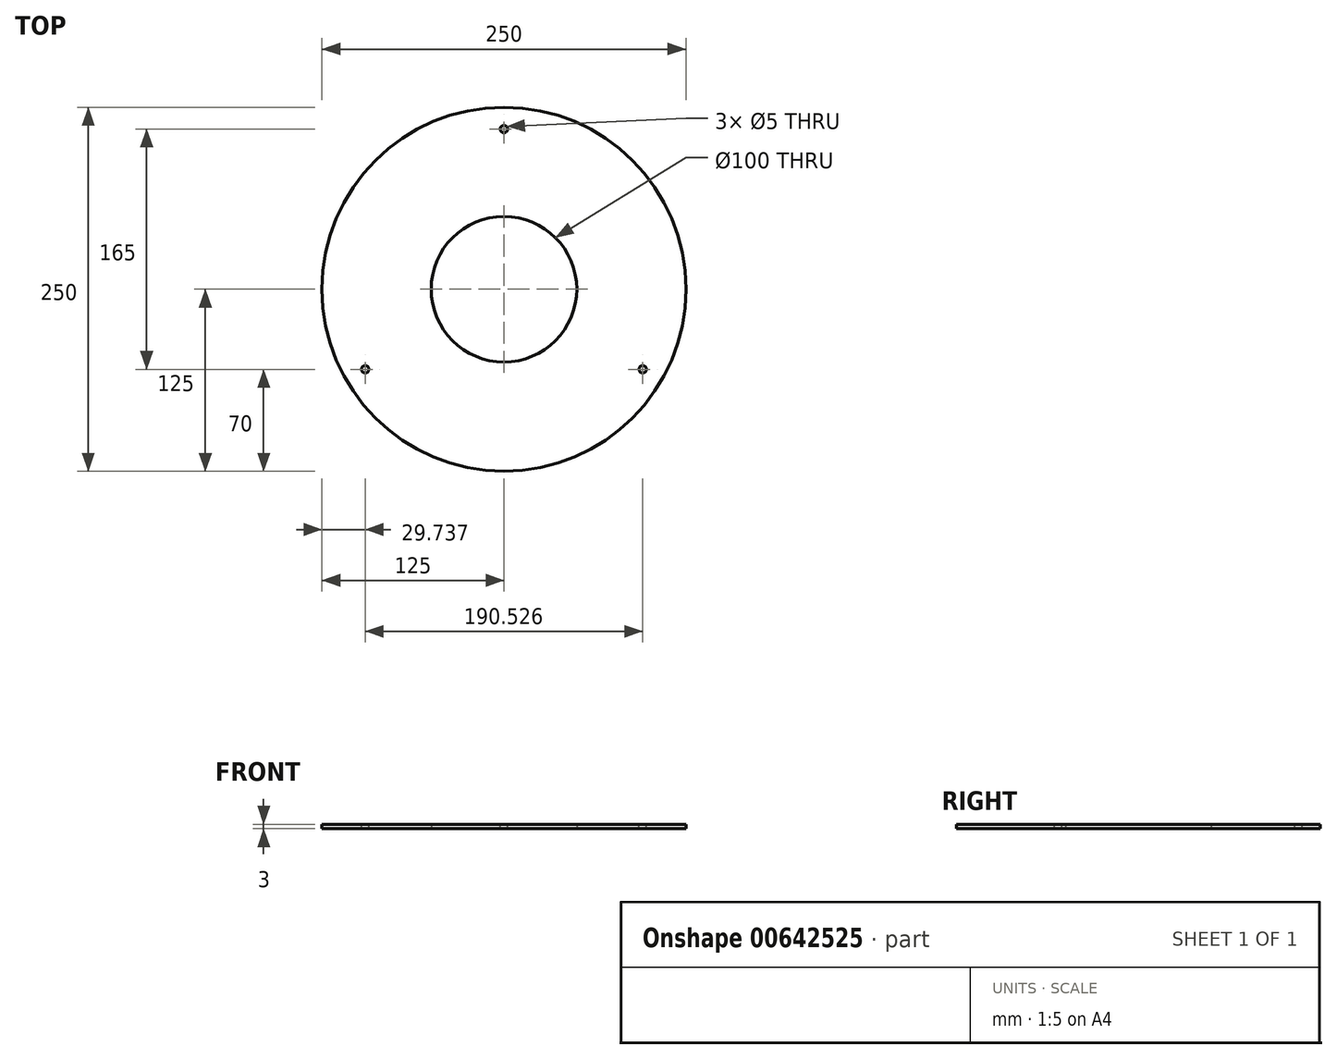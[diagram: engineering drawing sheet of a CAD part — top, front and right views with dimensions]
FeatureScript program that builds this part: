
annotation { "Feature Type Name" : "Feature", "Feature Type Description" : "" }
export const myFeature = defineFeature(function(context is Context, id is Id, definition is map)
    precondition{}
    {
        {
            var Q0;
            Q0=qCreatedBy(makeId("Top.planeOp"),FACE);
            var sketch = newSketch(context, id + "F0", { "sketchPlane" : qUnion([Q0])});
            skCircle(sketch, "E0", {"center": v(0, 0) * mm, "radius": 125 * mm});
            skCircle(sketch, "E1", {"center": v(0, 0) * mm, "radius": 50 * mm});
            skSolve(sketch);
        }
        {
            var Q0;
            Q0=makeQuery(id+"F0.imprint","IMPRINT",FACE,{"disambiguationData":[TD([[makeQuery(id+"F0.imprint","IMPRINT",EDGE,{"derivedFrom":sQuery(id+"F0.wireOp",EDGE,"E0")}),1.0]])]});
            extrude(context, id + "F1", {"entities" : qUnion([Q0]), "depth" : 3 * mm, "offsetDistance" : 25 * mm});
        }
        {
            var Q0;
            Q0=makeQuery(id+"F1.opExtrude","CAP_FACE",FACE,{"disambiguationData":[OSD([sQuery(id+"F0.wireOp",EDGE,"E0"),sQuery(id+"F0.wireOp",EDGE,"E1")])],"isStart":false});
            var sketch = newSketch(context, id + "F2", { "sketchPlane" : qUnion([Q0])});
            skPoint(sketch, "E2", {"position": v(0, 110) * mm});
            skPoint(sketch, "E3.center", {"position": v(0, 0) * mm});
            skLineSegment(sketch, "E3.anchor1", {"start": v(0, 0) * mm, "end": v(0, 110) * mm, "construction": true});
            skLineSegment(sketch, "E3.anchor2", {"start": v(0, 0) * mm, "end": v(0, 110) * mm, "construction": true});
            skPoint(sketch, "E4.1.0", {"position": v(-95.26, -55) * mm});
            skPoint(sketch, "E4.2.0", {"position": v(95.26, -55) * mm});
            skSolve(sketch);
        }
        {
            var Q0;
            Q0=sQuery(id+"F2.wireOp",VERTEX,"E2");
            var Q1;
            Q1=sQuery(id+"F2.wireOp",VERTEX,"E4.2.0");
            var Q2;
            Q2=sQuery(id+"F2.wireOp",VERTEX,"E4.1.0");
            var Q3;
            Q3=makeQuery(id+"F1.opExtrude","SWEPT_BODY",BODY,{"disambiguationData":[OSD([sQuery(id+"F0.wireOp",EDGE,"E0"),sQuery(id+"F0.wireOp",EDGE,"E1")])]});
            hole(context, id + "F3", {"style" : HoleStyle.SIMPLE, "endStyle" : HoleEndStyle.THROUGH, "holeDiameter" : 5 * mm, "majorDiameter" : 5 * mm, "isTappedThrough" : true, "tappedDepth" : 12 * mm, "tapClearance" : 3, "locations" : qUnion([Q0, Q1, Q2]), "scope" : qUnion([Q3])});
        }
    });
